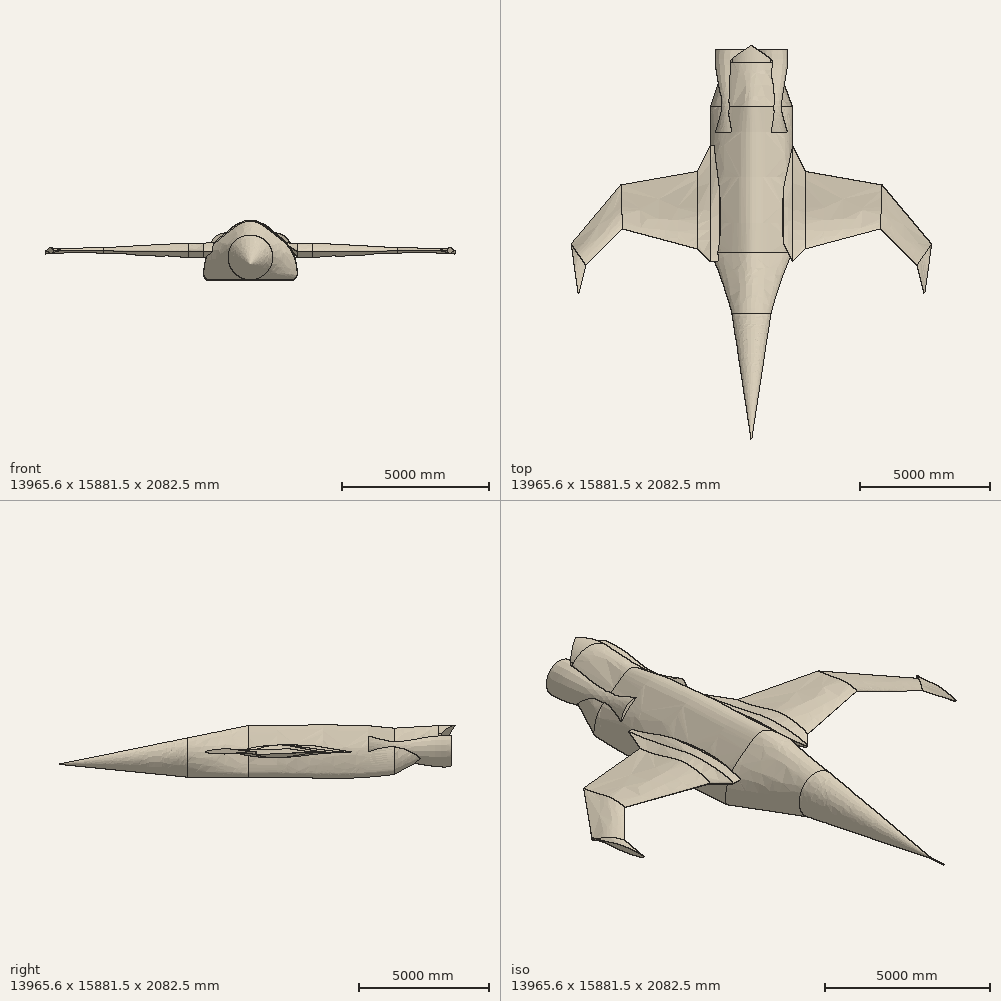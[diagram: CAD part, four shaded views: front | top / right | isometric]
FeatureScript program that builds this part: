
annotation { "Feature Type Name" : "Feature", "Feature Type Description" : "" }
export const myFeature = defineFeature(function(context is Context, id is Id, definition is map)
    precondition{}
    {
        {
            var Q0;
            Q0=qCreatedBy(makeId("Right.planeOp"),FACE);
            var sketch = newSketch(context, id + "F0", { "sketchPlane" : qUnion([Q0])});
            skLineSegment(sketch, "E0", {"start": v(0, 0) * mm, "end": v(-1750, 0) * mm});
            skLineSegment(sketch, "E1", {"start": v(-1750, 0) * mm, "end": v(-3500, 0) * mm});
            skLineSegment(sketch, "E2", {"start": v(-3500, 0) * mm, "end": v(-3500, -1000) * mm});
            skLineSegment(sketch, "E3", {"start": v(-3500, -1000) * mm, "end": v(-8500, -1000) * mm});
            skLineSegment(sketch, "E4", {"start": v(-8500, -1000) * mm, "end": v(-8500, -499.31) * mm});
            skLineSegment(sketch, "E5", {"start": v(-1151.4, 0) * mm, "end": v(-1151.4, 1000) * mm});
            skLineSegment(sketch, "E6", {"start": v(-1151.4, 1000) * mm, "end": v(-8500, -499.31) * mm});
            skLineSegment(sketch, "E7", {"start": v(-8500, -499.31) * mm, "end": v(-3500, -1000) * mm});
            skLineSegment(sketch, "E8", {"start": v(-3500, 0) * mm, "end": v(-3500, 520.82) * mm});
            skLineSegment(sketch, "E9", {"start": v(-8500, -499.31) * mm, "end": v(-8450, -499.31) * mm});
            skLineSegment(sketch, "E10", {"start": v(-8450, -499.31) * mm, "end": v(-8450, -489.1) * mm});
            skLineSegment(sketch, "E11", {"start": v(-8450, -499.31) * mm, "end": v(-8450, -504.32) * mm});
            skSolve(sketch);
        }
        {
            var Q0;
            Q0=sQuery(id+"F0.wireOp",EDGE,"E5");
            cPlane(context, id + "F1", {"entities" : qUnion([Q0]), "cplaneType" : CPlaneType.LINE_ANGLE, "offset" : 25 * mm, "angle" : 90 * degree, "oppositeDirection" : true, "width" : 150 * mm, "height" : 150 * mm});
        }
        {
            var Q0;
            Q0=qCreatedBy(id+"F1.planeOp",FACE);
            var sketch = newSketch(context, id + "F2", { "sketchPlane" : qUnion([Q0])});
            skLineSegment(sketch, "E12.top", {"start": v(-1394.2, -1000) * mm, "end": v(1394.2, -1000) * mm});
            skPoint(sketch, "E12.middle", {"position": v(0, 0) * mm});
            skFitSpline(sketch, "E13", {"points": [v(-1600, -1000) * mm, v(-848, 530) * mm, v(0, 1000) * mm, v(848, 530) * mm, v(1600, -1000) * mm], "startDerivative": vector(0, 10524.75) * mm, "endDerivative": vector(0, -10524.75) * mm});
            skArc(sketch, "E14", {"start": v(-735.27, 618.52) * mm, "mid": v(-1273.27, 435.52) * mm, "end": v(-1440.68, -107.53) * mm});
            skArc(sketch, "E15", {"start": v(1440.68, -107.53) * mm, "mid": v(1273.27, 435.52) * mm, "end": v(735.27, 618.52) * mm});
            skFitSpline(sketch, "E16.trimOffspring", {"points": [v(-1600, -1000) * mm, v(-848, 530) * mm, v(0, 1000) * mm, v(848, 530) * mm, v(1600, -1000) * mm], "startDerivative": vector(0, 10524.75) * mm, "endDerivative": vector(0, -10524.75) * mm});
            skFitSpline(sketch, "E17.trimOffspring", {"points": [v(-1600, -1000) * mm, v(-848, 530) * mm, v(0, 1000) * mm, v(848, 530) * mm, v(1600, -1000) * mm], "startDerivative": vector(0, 10524.75) * mm, "endDerivative": vector(0, -10524.75) * mm});
            skArc(sketch, "E18.filletArc", {"start": v(-1593.82, -787.83) * mm, "mid": v(-1539.85, -937.05) * mm, "end": v(-1394.2, -1000) * mm});
            skArc(sketch, "E19.filletArc", {"start": v(1394.2, -1000) * mm, "mid": v(1539.85, -937.05) * mm, "end": v(1593.82, -787.83) * mm});
            skSolve(sketch);
        }
        {
            var Q0;
            Q0=qCreatedBy(makeId("Front.planeOp"),FACE);
            var sketch = newSketch(context, id + "F3", { "sketchPlane" : qUnion([Q0])});
            skLineSegment(sketch, "E20.top", {"start": v(-1394.2, -1000) * mm, "end": v(1394.2, -1000) * mm});
            skPoint(sketch, "E20.middle", {"position": v(0, 0) * mm});
            skFitSpline(sketch, "E21", {"points": [v(-1600, -1000) * mm, v(-848, 530) * mm, v(0, 1000) * mm, v(848, 530) * mm, v(1600, -1000) * mm], "startDerivative": vector(0, 10524.75) * mm, "endDerivative": vector(0, -10524.75) * mm});
            skArc(sketch, "E22", {"start": v(-735.27, 618.52) * mm, "mid": v(-1273.27, 435.52) * mm, "end": v(-1440.68, -107.53) * mm});
            skArc(sketch, "E23", {"start": v(1440.68, -107.53) * mm, "mid": v(1273.27, 435.52) * mm, "end": v(735.27, 618.52) * mm});
            skFitSpline(sketch, "E24.trimOffspring", {"points": [v(-1600, -1000) * mm, v(-848, 530) * mm, v(0, 1000) * mm, v(848, 530) * mm, v(1600, -1000) * mm], "startDerivative": vector(0, 10524.75) * mm, "endDerivative": vector(0, -10524.75) * mm});
            skFitSpline(sketch, "E25.trimOffspring", {"points": [v(-1600, -1000) * mm, v(-848, 530) * mm, v(0, 1000) * mm, v(848, 530) * mm, v(1600, -1000) * mm], "startDerivative": vector(0, 10524.75) * mm, "endDerivative": vector(0, -10524.75) * mm});
            skArc(sketch, "E26.filletArc", {"start": v(-1593.82, -787.83) * mm, "mid": v(-1539.85, -937.05) * mm, "end": v(-1394.2, -1000) * mm});
            skArc(sketch, "E27.filletArc", {"start": v(1394.2, -1000) * mm, "mid": v(1539.85, -937.05) * mm, "end": v(1593.82, -787.83) * mm});
            skSolve(sketch);
        }
        {
            var Q0;
            Q0=qCreatedBy(makeId("Front.planeOp"),FACE);
            cPlane(context, id + "F4", {"entities" : qUnion([Q0]), "cplaneType" : CPlaneType.OFFSET, "offset" : 3500 * mm, "oppositeDirection" : true, "width" : 150 * mm, "height" : 150 * mm});
        }
        {
            var Q0;
            Q0=qCreatedBy(id+"F4.planeOp",FACE);
            var sketch = newSketch(context, id + "F5", { "sketchPlane" : qUnion([Q0])});
            skLineSegment(sketch, "E28.top", {"start": v(-1394.2, -1000) * mm, "end": v(1394.2, -1000) * mm});
            skPoint(sketch, "E28.middle", {"position": v(0, 0) * mm});
            skFitSpline(sketch, "E29", {"points": [v(-1600, -1000) * mm, v(-848, 530) * mm, v(0, 1000) * mm, v(848, 530) * mm, v(1600, -1000) * mm], "startDerivative": vector(0, 10524.75) * mm, "endDerivative": vector(0, -10524.75) * mm});
            skArc(sketch, "E30", {"start": v(-735.27, 618.52) * mm, "mid": v(-1273.27, 435.52) * mm, "end": v(-1440.68, -107.53) * mm});
            skArc(sketch, "E31", {"start": v(1440.68, -107.53) * mm, "mid": v(1273.27, 435.52) * mm, "end": v(735.27, 618.52) * mm});
            skFitSpline(sketch, "E32.trimOffspring", {"points": [v(-1600, -1000) * mm, v(-848, 530) * mm, v(0, 1000) * mm, v(848, 530) * mm, v(1600, -1000) * mm], "startDerivative": vector(0, 10524.75) * mm, "endDerivative": vector(0, -10524.75) * mm});
            skFitSpline(sketch, "E33.trimOffspring", {"points": [v(-1600, -1000) * mm, v(-848, 530) * mm, v(0, 1000) * mm, v(848, 530) * mm, v(1600, -1000) * mm], "startDerivative": vector(0, 10524.75) * mm, "endDerivative": vector(0, -10524.75) * mm});
            skArc(sketch, "E34.filletArc", {"start": v(-1593.82, -787.83) * mm, "mid": v(-1539.85, -937.05) * mm, "end": v(-1394.2, -1000) * mm});
            skArc(sketch, "E35.filletArc", {"start": v(1394.2, -1000) * mm, "mid": v(1539.85, -937.05) * mm, "end": v(1593.82, -787.83) * mm});
            skSolve(sketch);
        }
        {
            var Q0;
            Q0=qCreatedBy(makeId("Front.planeOp"),FACE);
            cPlane(context, id + "F6", {"entities" : qUnion([Q0]), "cplaneType" : CPlaneType.OFFSET, "offset" : 4500 * mm, "oppositeDirection" : true, "width" : 150 * mm, "height" : 150 * mm});
        }
        {
            var Q0;
            Q0=qCreatedBy(id+"F6.planeOp",FACE);
            var sketch = newSketch(context, id + "F7", { "sketchPlane" : qUnion([Q0])});
            skLineSegment(sketch, "E36.top", {"start": v(-1413.07, -900) * mm, "end": v(1413.07, -900) * mm});
            skPoint(sketch, "E36.middle", {"position": v(0, 0) * mm});
            skFitSpline(sketch, "E37", {"points": [v(-1600, -900) * mm, v(-784.42, 441.24) * mm, v(0, 900) * mm, v(784.42, 441.24) * mm, v(1600, -900) * mm], "startDerivative": vector(0, 9508.62) * mm, "endDerivative": vector(0, -9508.62) * mm});
            skArc(sketch, "E38", {"start": v(-719.25, 488.69) * mm, "mid": v(-1131.76, 394.84) * mm, "end": v(-1324.66, 18.33) * mm});
            skArc(sketch, "E39", {"start": v(1324.66, 18.33) * mm, "mid": v(1131.76, 394.84) * mm, "end": v(719.25, 488.69) * mm});
            skFitSpline(sketch, "E40.trimOffspring", {"points": [v(-1600, -900) * mm, v(-784.42, 441.24) * mm, v(0, 900) * mm, v(784.42, 441.24) * mm, v(1600, -900) * mm], "startDerivative": vector(0, 9508.62) * mm, "endDerivative": vector(0, -9508.62) * mm});
            skFitSpline(sketch, "E41.trimOffspring", {"points": [v(-1600, -900) * mm, v(-784.42, 441.24) * mm, v(0, 900) * mm, v(784.42, 441.24) * mm, v(1600, -900) * mm], "startDerivative": vector(0, 9508.62) * mm, "endDerivative": vector(0, -9508.62) * mm});
            skArc(sketch, "E42.filletArc", {"start": v(-1592.48, -705.43) * mm, "mid": v(-1545.4, -842.02) * mm, "end": v(-1413.07, -900) * mm});
            skArc(sketch, "E43.filletArc", {"start": v(1413.07, -900) * mm, "mid": v(1545.4, -842.02) * mm, "end": v(1592.48, -705.43) * mm});
            skLineSegment(sketch, "E44", {"start": v(-719.25, 488.69) * mm, "end": v(-1324.66, 18.33) * mm, "construction": true});
            skLineSegment(sketch, "E45", {"start": v(719.25, 488.69) * mm, "end": v(1324.66, 18.33) * mm, "construction": true});
            skSolve(sketch);
        }
        {
            var Q0;
            Q0=qCreatedBy(makeId("Front.planeOp"),FACE);
            cPlane(context, id + "F8", {"entities" : qUnion([Q0]), "cplaneType" : CPlaneType.OFFSET, "offset" : 6232.05 * mm, "oppositeDirection" : true, "width" : 150 * mm, "height" : 150 * mm});
        }
        {
            var Q0;
            Q0=qCreatedBy(id+"F8.planeOp",FACE);
            var sketch = newSketch(context, id + "F9", { "sketchPlane" : qUnion([Q0])});
            skArc(sketch, "E46", {"start": v(998.61, 52.63) * mm, "mid": v(0, 1000) * mm, "end": v(-998.61, 52.63) * mm});
            skLineSegment(sketch, "E47", {"start": v(0, 0) * mm, "end": v(-948.68, 0) * mm});
            skLineSegment(sketch, "E48", {"start": v(0, 0) * mm, "end": v(948.68, 0) * mm});
            skLineSegment(sketch, "E49", {"start": v(0, 1000) * mm, "end": v(0, 675) * mm, "construction": true});
            skLineSegment(sketch, "E50", {"start": v(0, 675) * mm, "end": v(-737.82, 675) * mm, "construction": true});
            skLineSegment(sketch, "E51", {"start": v(0, 675) * mm, "end": v(737.82, 675) * mm, "construction": true});
            skPoint(sketch, "E52.visualSharp", {"position": v(-1000, 0) * mm});
            skArc(sketch, "E52.filletArc", {"start": v(-998.61, 52.63) * mm, "mid": v(-984.96, 15.59) * mm, "end": v(-948.68, 0) * mm});
            skPoint(sketch, "E53.visualSharp", {"position": v(1000, 0) * mm});
            skArc(sketch, "E53.filletArc", {"start": v(948.68, 0) * mm, "mid": v(984.96, 15.59) * mm, "end": v(998.61, 52.63) * mm});
            skSolve(sketch);
        }
        {
            var Q0;
            Q0=makeQuery(id+"F2.imprint","IMPRINT",FACE,{"disambiguationData":[TD([[makeQuery(id+"F2.imprint","IMPRINT",EDGE,{"derivedFrom":sQuery(id+"F2.wireOp",EDGE,"E12.top")}),1.0]])]});
            var Q1;
            Q1=makeQuery(id+"F3.imprint","IMPRINT",FACE,{"disambiguationData":[TD([[makeQuery(id+"F3.imprint","IMPRINT",EDGE,{"derivedFrom":sQuery(id+"F3.wireOp",EDGE,"E20.top")}),1.0]])]});
            var Q2;
            Q2=makeQuery(id+"F5.imprint","IMPRINT",FACE,{"disambiguationData":[TD([[makeQuery(id+"F5.imprint","IMPRINT",EDGE,{"derivedFrom":sQuery(id+"F5.wireOp",EDGE,"E28.top")}),1.0]])]});
            var Q3;
            Q3=makeQuery(id+"F7.imprint","IMPRINT",FACE,{"disambiguationData":[TD([[makeQuery(id+"F7.imprint","IMPRINT",EDGE,{"derivedFrom":sQuery(id+"F7.wireOp",EDGE,"E36.top")}),1.0]])]});
            loft(context, id + "F10", {"sheetProfilesArray" : [{ "sheetProfileEntities" : qUnion([Q0]) }, { "sheetProfileEntities" : qUnion([Q1]) }, { "sheetProfileEntities" : qUnion([Q2]) }, { "sheetProfileEntities" : qUnion([Q3]) }]});
        }
        {
            var Q0;
            Q0=sQuery(id+"F7.wireOp",EDGE,"E44");
            var Q1;
            Q1=sQuery(id+"F9.wireOp",VERTEX,"E50.end");
            cPlane(context, id + "F11", {"entities" : qUnion([Q0, Q1]), "cplaneType" : CPlaneType.LINE_ANGLE, "offset" : 25 * mm, "angle" : 180 * degree, "width" : 150 * mm, "height" : 150 * mm});
        }
        {
            var Q0;
            Q0=qCreatedBy(id+"F11.planeOp",FACE);
            var sketch = newSketch(context, id + "F12", { "sketchPlane" : qUnion([Q0])});
            skLineSegment(sketch, "E54", {"start": v(-589.34, 4526.34) * mm, "end": v(-612.8, 6268.32) * mm});
            skLineSegment(sketch, "E55", {"start": v(-1354.08, 4472.19) * mm, "end": v(-612.8, 6268.32) * mm});
            skSolve(sketch);
        }
        {
            var Q0;
            Q0=sQuery(id+"F7.wireOp",EDGE,"E45");
            var Q1;
            Q1=sQuery(id+"F9.wireOp",VERTEX,"E51.end");
            cPlane(context, id + "F13", {"entities" : qUnion([Q0, Q1]), "cplaneType" : CPlaneType.LINE_ANGLE, "offset" : 25 * mm, "angle" : 0 * degree, "width" : 150 * mm, "height" : 150 * mm});
        }
        {
            var Q0;
            Q0=qCreatedBy(id+"F13.planeOp",FACE);
            var sketch = newSketch(context, id + "F14", { "sketchPlane" : qUnion([Q0])});
            skLineSegment(sketch, "E56", {"start": v(589.34, 4526.34) * mm, "end": v(612.8, 6268.32) * mm});
            skLineSegment(sketch, "E57", {"start": v(1354.08, 4472.19) * mm, "end": v(612.8, 6268.32) * mm});
            skSolve(sketch);
        }
        {
            var Q1;
            Q1=makeQuery(id+"F10.opLoft","CAP_FACE",FACE,{"disambiguationData":[OSD([makeQuery(id+"F7.imprint","IMPRINT",FACE,{"disambiguationData":[TD([[makeQuery(id+"F7.imprint","IMPRINT",EDGE,{"derivedFrom":sQuery(id+"F7.wireOp",EDGE,"E36.top")}),1.0]])]})])],"isStart":true});
            var Q2;
            Q2=makeQuery(id+"F9.imprint","IMPRINT",FACE,{"disambiguationData":[TD([[makeQuery(id+"F9.imprint","IMPRINT",EDGE,{"derivedFrom":sQuery(id+"F9.wireOp",EDGE,"E46")}),1.0]])]});
            var Q3;
            Q3=sQuery(id+"F12.wireOp",EDGE,"E54");
            var Q4;
            Q4=sQuery(id+"F14.wireOp",EDGE,"E56");
            loft(context, id + "F15", {"operationType" : NewBodyOperationType.ADD, "addGuides" : true, "sheetProfilesArray" : [{ "sheetProfileEntities" : qUnion([Q1]) }, { "sheetProfileEntities" : qUnion([Q2]) }], "guidesArray" : [{ "guideEntities" : qUnion([Q3]), "guideDerivativeType" : LoftGuideDerivativeType.DEFAULT, "guideDerivativeMagnitude" : 1 }, { "guideEntities" : qUnion([Q4]), "guideDerivativeType" : LoftGuideDerivativeType.DEFAULT, "guideDerivativeMagnitude" : 1 }]});
        }
        {
            var Q0;
            Q0=makeQuery(id+"F15.opLoft","CAP_FACE",FACE,{"disambiguationData":[OSD([makeQuery(id+"F9.imprint","IMPRINT",FACE,{"disambiguationData":[TD([[makeQuery(id+"F9.imprint","IMPRINT",EDGE,{"derivedFrom":sQuery(id+"F9.wireOp",EDGE,"E46")}),1.0]])]})])],"isStart":true});
            extrude(context, id + "F16", {"entities" : qUnion([Q0]), "operationType" : NewBodyOperationType.ADD, "depth" : 649.4 * mm, "offsetDistance" : 25 * mm});
        }
        {
            var Q0;
            Q0=qCreatedBy(makeId("Right.planeOp"),FACE);
            var sketch = newSketch(context, id + "F17", { "sketchPlane" : qUnion([Q0])});
            skLineSegment(sketch, "E58", {"start": v(0, 0) * mm, "end": v(4500, 0) * mm});
            skLineSegment(sketch, "E59", {"start": v(4500, 0) * mm, "end": v(6232.05, 0) * mm});
            skLineSegment(sketch, "E60", {"start": v(4500, 0) * mm, "end": v(4500, 1000) * mm});
            skLineSegment(sketch, "E61", {"start": v(4500, 1000) * mm, "end": v(6881.46, 1000) * mm});
            skLineSegment(sketch, "E62", {"start": v(6881.46, 1000) * mm, "end": v(6881.46, -1000) * mm});
            skLineSegment(sketch, "E63", {"start": v(6881.46, 1000) * mm, "end": v(6232.05, 0) * mm});
            skLineSegment(sketch, "E64", {"start": v(6232.05, 0) * mm, "end": v(5582.64, -1000) * mm});
            skLineSegment(sketch, "E65", {"start": v(5582.64, -1000) * mm, "end": v(6881.46, -1000) * mm});
            skSolve(sketch);
        }
        {
            var Q0;
            Q0=makeQuery(id+"F17.imprint","IMPRINT",FACE,{"disambiguationData":[TD([[makeQuery(id+"F17.imprint","IMPRINT",EDGE,{"derivedFrom":sQuery(id+"F17.wireOp",EDGE,"E62")}),-1.0]])]});
            var Q1;
            Q1=sQuery(id+"F17.wireOp",EDGE,"E61");
            revolve(context, id + "F18", {"operationType" : NewBodyOperationType.REMOVE, "entities" : qUnion([Q0]), "axis" : qUnion([Q1]), "revolveType" : RevolveType.SYMMETRIC, "oppositeDirection" : true, "angle" : 182 * degree});
        }
        {
            var Q0;
            Q0=qCreatedBy(id+"F1.planeOp",FACE);
            var sketch = newSketch(context, id + "F19", { "sketchPlane" : qUnion([Q0])});
            skLineSegment(sketch, "E66.top", {"start": v(-1394.2, -1000) * mm, "end": v(1394.2, -1000) * mm});
            skPoint(sketch, "E66.middle", {"position": v(0, 0) * mm});
            skFitSpline(sketch, "E67", {"points": [v(-1600, -1000) * mm, v(-848, 530) * mm, v(0, 1000) * mm, v(848, 530) * mm, v(1600, -1000) * mm], "startDerivative": vector(0, 10524.75) * mm, "endDerivative": vector(0, -10524.75) * mm});
            skArc(sketch, "E68.filletArc", {"start": v(-1593.82, -787.83) * mm, "mid": v(-1539.85, -937.05) * mm, "end": v(-1394.2, -1000) * mm});
            skArc(sketch, "E69.filletArc", {"start": v(1394.2, -1000) * mm, "mid": v(1539.85, -937.05) * mm, "end": v(1593.82, -787.83) * mm});
            skLineSegment(sketch, "E70", {"start": v(-1593.82, -787.83) * mm, "end": v(-1394.2, -1000) * mm, "construction": true});
            skLineSegment(sketch, "E71", {"start": v(1593.82, -787.83) * mm, "end": v(1394.2, -1000) * mm, "construction": true});
            skSolve(sketch);
        }
        {
            var Q0;
            Q0=qCreatedBy(makeId("Front.planeOp"),FACE);
            cPlane(context, id + "F20", {"entities" : qUnion([Q0]), "cplaneType" : CPlaneType.OFFSET, "offset" : 3500 * mm, "width" : 150 * mm, "height" : 150 * mm});
        }
        {
            var Q0;
            Q0=qCreatedBy(id+"F20.planeOp",FACE);
            var sketch = newSketch(context, id + "F21", { "sketchPlane" : qUnion([Q0])});
            skCircle(sketch, "E72", {"center": v(0, -239.59) * mm, "radius": 760.41 * mm});
            skLineSegment(sketch, "E73", {"start": v(0, -1000) * mm, "end": v(0, -800) * mm, "construction": true});
            skLineSegment(sketch, "E74", {"start": v(0, -800) * mm, "end": v(-513.97, -800) * mm, "construction": true});
            skLineSegment(sketch, "E75", {"start": v(0, -800) * mm, "end": v(513.97, -800) * mm, "construction": true});
            skSolve(sketch);
        }
        {
            var Q0;
            Q0=qCreatedBy(makeId("Front.planeOp"),FACE);
            cPlane(context, id + "F22", {"entities" : qUnion([Q0]), "cplaneType" : CPlaneType.OFFSET, "offset" : 8450 * mm, "width" : 150 * mm, "height" : 150 * mm});
        }
        {
            var Q0;
            Q0=qCreatedBy(id+"F22.planeOp",FACE);
            var sketch = newSketch(context, id + "F23", { "sketchPlane" : qUnion([Q0])});
            skCircle(sketch, "E76", {"center": v(0, -496.71) * mm, "radius": 7.6 * mm});
            skSolve(sketch);
        }
        {
            var Q0;
            Q0=sQuery(id+"F19.wireOp",EDGE,"E70");
            var Q1;
            Q1=sQuery(id+"F21.wireOp",VERTEX,"E74.end");
            cPlane(context, id + "F24", {"entities" : qUnion([Q0, Q1]), "cplaneType" : CPlaneType.LINE_ANGLE, "offset" : 25 * mm, "angle" : 0 * degree, "width" : 150 * mm, "height" : 150 * mm});
        }
        {
            var Q0;
            Q0=qCreatedBy(id+"F24.planeOp",FACE);
            var sketch = newSketch(context, id + "F25", { "sketchPlane" : qUnion([Q0])});
            skLineSegment(sketch, "E77", {"start": v(3032.27, -230.44) * mm, "end": v(558.11, 518.4) * mm});
            skLineSegment(sketch, "E78", {"start": v(3032.27, -230.44) * mm, "end": v(558.11, 227.09) * mm});
            skSolve(sketch);
        }
        {
            var Q0;
            Q0=sQuery(id+"F19.wireOp",EDGE,"E71");
            var Q1;
            Q1=sQuery(id+"F21.wireOp",VERTEX,"E75.end");
            cPlane(context, id + "F26", {"entities" : qUnion([Q0, Q1]), "cplaneType" : CPlaneType.LINE_ANGLE, "offset" : 25 * mm, "angle" : 180 * degree, "width" : 150 * mm, "height" : 150 * mm});
        }
        {
            var Q0;
            Q0=qCreatedBy(id+"F26.planeOp",FACE);
            var sketch = newSketch(context, id + "F27", { "sketchPlane" : qUnion([Q0])});
            skLineSegment(sketch, "E79", {"start": v(-3032.27, -230.44) * mm, "end": v(-558.11, 518.4) * mm});
            skLineSegment(sketch, "E80", {"start": v(-3032.27, -230.44) * mm, "end": v(-558.11, 227.09) * mm});
            skSolve(sketch);
        }
        {
            var Q1;
            Q1=makeQuery(id+"F19.imprint","IMPRINT",FACE,{"disambiguationData":[TD([[makeQuery(id+"F19.imprint","IMPRINT",EDGE,{"derivedFrom":sQuery(id+"F19.wireOp",EDGE,"E66.top")}),1.0]])]});
            var Q2;
            Q2=makeQuery(id+"F21.imprint","IMPRINT",FACE,{"disambiguationData":[TD([[makeQuery(id+"F21.imprint","IMPRINT",EDGE,{"derivedFrom":sQuery(id+"F21.wireOp",EDGE,"E72")}),1.0]])]});
            var Q3;
            Q3=sQuery(id+"F25.wireOp",EDGE,"E77");
            var Q4;
            Q4=sQuery(id+"F27.wireOp",EDGE,"E79");
            loft(context, id + "F28", {"operationType" : NewBodyOperationType.ADD, "addGuides" : true, "sheetProfilesArray" : [{ "sheetProfileEntities" : qUnion([Q1]) }, { "sheetProfileEntities" : qUnion([Q2]) }], "guidesArray" : [{ "guideEntities" : qUnion([Q3]), "guideDerivativeType" : LoftGuideDerivativeType.DEFAULT, "guideDerivativeMagnitude" : 1 }, { "guideEntities" : qUnion([Q4]), "guideDerivativeType" : LoftGuideDerivativeType.DEFAULT, "guideDerivativeMagnitude" : 1 }]});
        }
        {
            var Q1;
            Q1=makeQuery(id+"F28.opLoft","CAP_FACE",FACE,{"disambiguationData":[OSD([makeQuery(id+"F21.imprint","IMPRINT",FACE,{"disambiguationData":[TD([[makeQuery(id+"F21.imprint","IMPRINT",EDGE,{"derivedFrom":sQuery(id+"F21.wireOp",EDGE,"E72")}),1.0]])]})])],"isStart":true});
            var Q2;
            Q2=makeQuery(id+"F23.imprint","IMPRINT",FACE,{"disambiguationData":[TD([[makeQuery(id+"F23.imprint","IMPRINT",EDGE,{"derivedFrom":sQuery(id+"F23.wireOp",EDGE,"E76")}),1.0]])]});
            loft(context, id + "F29", {"operationType" : NewBodyOperationType.ADD, "sheetProfilesArray" : [{ "sheetProfileEntities" : qUnion([Q1]) }, { "sheetProfileEntities" : qUnion([Q2]) }]});
        }
        {
            var Q0;
            Q0=makeQuery(id+"F29.opLoft","CAP_FACE",FACE,{"disambiguationData":[OSD([makeQuery(id+"F23.imprint","IMPRINT",FACE,{"disambiguationData":[TD([[makeQuery(id+"F23.imprint","IMPRINT",EDGE,{"derivedFrom":sQuery(id+"F23.wireOp",EDGE,"E76")}),1.0]])]})])],"isStart":true});
            extrude(context, id + "F30", {"entities" : qUnion([Q0]), "operationType" : NewBodyOperationType.ADD, "depth" : 550 * mm, "offsetDistance" : 25 * mm});
        }
        {
            var Q0;
            Q0=qCreatedBy(makeId("Front.planeOp"),FACE);
            cPlane(context, id + "F31", {"entities" : qUnion([Q0]), "cplaneType" : CPlaneType.OFFSET, "offset" : 3500 * mm, "oppositeDirection" : true, "width" : 150 * mm, "height" : 150 * mm});
        }
        {
            var Q0;
            Q0=qCreatedBy(id+"F31.planeOp",FACE);
            var sketch = newSketch(context, id + "F32", { "sketchPlane" : qUnion([Q0])});
            skCircle(sketch, "E81", {"center": v(-800, 0) * mm, "radius": 600 * mm});
            skCircle(sketch, "E82", {"center": v(800, 0) * mm, "radius": 600 * mm});
            skSolve(sketch);
        }
        {
            var Q0;
            Q0=qCreatedBy(makeId("Front.planeOp"),FACE);
            cPlane(context, id + "F33", {"entities" : qUnion([Q0]), "cplaneType" : CPlaneType.OFFSET, "offset" : 4500 * mm, "oppositeDirection" : true, "width" : 150 * mm, "height" : 150 * mm});
        }
        {
            var Q0;
            Q0=qCreatedBy(id+"F33.planeOp",FACE);
            var sketch = newSketch(context, id + "F34", { "sketchPlane" : qUnion([Q0])});
            skCircle(sketch, "E83", {"center": v(-800, 0) * mm, "radius": 400 * mm});
            skCircle(sketch, "E84", {"center": v(800, 0) * mm, "radius": 400 * mm});
            skSolve(sketch);
        }
        {
            var Q0;
            Q0=qCreatedBy(makeId("Front.planeOp"),FACE);
            cPlane(context, id + "F35", {"entities" : qUnion([Q0]), "cplaneType" : CPlaneType.OFFSET, "offset" : 6232.05 * mm, "oppositeDirection" : true, "width" : 150 * mm, "height" : 150 * mm});
        }
        {
            var Q0;
            Q0=qCreatedBy(id+"F35.planeOp",FACE);
            var sketch = newSketch(context, id + "F36", { "sketchPlane" : qUnion([Q0])});
            skCircle(sketch, "E85", {"center": v(-800, 0) * mm, "radius": 600 * mm});
            skCircle(sketch, "E86", {"center": v(800, 0) * mm, "radius": 600 * mm});
            skSolve(sketch);
        }
        {
            var Q0;
            Q0=qCreatedBy(makeId("Front.planeOp"),FACE);
            cPlane(context, id + "F37", {"entities" : qUnion([Q0]), "cplaneType" : CPlaneType.OFFSET, "offset" : 6732.05 * mm, "oppositeDirection" : true, "width" : 150 * mm, "height" : 150 * mm});
        }
        {
            var Q0;
            Q0=qCreatedBy(id+"F37.planeOp",FACE);
            var sketch = newSketch(context, id + "F38", { "sketchPlane" : qUnion([Q0])});
            skCircle(sketch, "E87", {"center": v(-800, 0) * mm, "radius": 600 * mm});
            skCircle(sketch, "E88", {"center": v(800, 0) * mm, "radius": 600 * mm});
            skSolve(sketch);
        }
        {
            var Q0;
            Q0=makeQuery(id+"F32.imprint","IMPRINT",FACE,{"disambiguationData":[TD([[makeQuery(id+"F32.imprint","IMPRINT",EDGE,{"derivedFrom":sQuery(id+"F32.wireOp",EDGE,"E81")}),1.0]])]});
            var Q1;
            Q1=makeQuery(id+"F34.imprint","IMPRINT",FACE,{"disambiguationData":[TD([[makeQuery(id+"F34.imprint","IMPRINT",EDGE,{"derivedFrom":sQuery(id+"F34.wireOp",EDGE,"E83")}),1.0]])]});
            var Q2;
            Q2=makeQuery(id+"F36.imprint","IMPRINT",FACE,{"disambiguationData":[TD([[makeQuery(id+"F36.imprint","IMPRINT",EDGE,{"derivedFrom":sQuery(id+"F36.wireOp",EDGE,"E85")}),1.0]])]});
            var Q3;
            Q3=makeQuery(id+"F38.imprint","IMPRINT",FACE,{"disambiguationData":[TD([[makeQuery(id+"F38.imprint","IMPRINT",EDGE,{"derivedFrom":sQuery(id+"F38.wireOp",EDGE,"E87")}),1.0]])]});
            loft(context, id + "F39", {"sheetProfilesArray" : [{ "sheetProfileEntities" : qUnion([Q0]) }, { "sheetProfileEntities" : qUnion([Q1]) }, { "sheetProfileEntities" : qUnion([Q2]) }, { "sheetProfileEntities" : qUnion([Q3]) }]});
        }
        {
            var Q0;
            Q0=makeQuery(id+"F32.imprint","IMPRINT",FACE,{"disambiguationData":[TD([[makeQuery(id+"F32.imprint","IMPRINT",EDGE,{"derivedFrom":sQuery(id+"F32.wireOp",EDGE,"E82")}),1.0]])]});
            var Q1;
            Q1=makeQuery(id+"F34.imprint","IMPRINT",FACE,{"disambiguationData":[TD([[makeQuery(id+"F34.imprint","IMPRINT",EDGE,{"derivedFrom":sQuery(id+"F34.wireOp",EDGE,"E84")}),1.0]])]});
            var Q2;
            Q2=makeQuery(id+"F36.imprint","IMPRINT",FACE,{"disambiguationData":[TD([[makeQuery(id+"F36.imprint","IMPRINT",EDGE,{"derivedFrom":sQuery(id+"F36.wireOp",EDGE,"E86")}),1.0]])]});
            var Q3;
            Q3=makeQuery(id+"F38.imprint","IMPRINT",FACE,{"disambiguationData":[TD([[makeQuery(id+"F38.imprint","IMPRINT",EDGE,{"derivedFrom":sQuery(id+"F38.wireOp",EDGE,"E88")}),1.0]])]});
            loft(context, id + "F40", {"sheetProfilesArray" : [{ "sheetProfileEntities" : qUnion([Q0]) }, { "sheetProfileEntities" : qUnion([Q1]) }, { "sheetProfileEntities" : qUnion([Q2]) }, { "sheetProfileEntities" : qUnion([Q3]) }]});
        }
        {
            var Q0;
            Q0=qCreatedBy(makeId("Top.planeOp"),FACE);
            var sketch = newSketch(context, id + "F41", { "sketchPlane" : qUnion([Q0])});
            skLineSegment(sketch, "E89", {"start": v(0, 0) * mm, "end": v(-1250, 0) * mm});
            skLineSegment(sketch, "E90", {"start": v(-1250, 0) * mm, "end": v(-2100, 0) * mm});
            skLineSegment(sketch, "E91", {"start": v(-2100, 0) * mm, "end": v(-2100, -1000) * mm});
            skLineSegment(sketch, "E92", {"start": v(-2100, 0) * mm, "end": v(-2100, 2000) * mm});
            skLineSegment(sketch, "E93", {"start": v(-2100, -1000) * mm, "end": v(-4997.78, -223.54) * mm});
            skLineSegment(sketch, "E94", {"start": v(-2100, 2000) * mm, "end": v(-5054.42, 1479.06) * mm});
            skLineSegment(sketch, "E95", {"start": v(-4997.78, -223.54) * mm, "end": v(-5054.42, 1479.06) * mm});
            skLineSegment(sketch, "E96", {"start": v(-4997.78, -223.54) * mm, "end": v(-6412, -1637.76) * mm});
            skLineSegment(sketch, "E97", {"start": v(-5054.42, 1479.06) * mm, "end": v(-6982.79, -819.08) * mm});
            skLineSegment(sketch, "E98", {"start": v(-6412, -1637.76) * mm, "end": v(-6982.79, -819.08) * mm});
            skLineSegment(sketch, "E99", {"start": v(-6412, -1637.76) * mm, "end": v(-6704.44, -2799.61) * mm});
            skLineSegment(sketch, "E100", {"start": v(-6704.44, -2799.61) * mm, "end": v(-6982.79, -819.08) * mm});
            skLineSegment(sketch, "E101", {"start": v(0, 0) * mm, "end": v(1250, 0) * mm});
            skLineSegment(sketch, "E102", {"start": v(1250, 0) * mm, "end": v(2100, 0) * mm});
            skLineSegment(sketch, "E103", {"start": v(2100, 0) * mm, "end": v(2100, -1000) * mm});
            skLineSegment(sketch, "E104", {"start": v(2100, 0) * mm, "end": v(2100, 2000) * mm});
            skLineSegment(sketch, "E105", {"start": v(2100, -1000) * mm, "end": v(4997.78, -223.54) * mm});
            skLineSegment(sketch, "E106", {"start": v(2100, 2000) * mm, "end": v(5054.42, 1479.06) * mm});
            skLineSegment(sketch, "E107", {"start": v(4997.78, -223.54) * mm, "end": v(5054.42, 1479.06) * mm});
            skLineSegment(sketch, "E108", {"start": v(4997.78, -223.54) * mm, "end": v(6412, -1637.76) * mm});
            skLineSegment(sketch, "E109", {"start": v(5054.42, 1479.06) * mm, "end": v(6982.79, -819.08) * mm});
            skLineSegment(sketch, "E110", {"start": v(6412, -1637.76) * mm, "end": v(6982.79, -819.08) * mm});
            skLineSegment(sketch, "E111", {"start": v(6412, -1637.76) * mm, "end": v(6704.44, -2799.61) * mm});
            skLineSegment(sketch, "E112", {"start": v(6704.44, -2799.61) * mm, "end": v(6982.79, -819.08) * mm});
            skSolve(sketch);
        }
        {
            var Q0;
            Q0=qCreatedBy(makeId("Right.planeOp"),FACE);
            var sketch = newSketch(context, id + "F42", { "sketchPlane" : qUnion([Q0])});
            skFitSpline(sketch, "E113", {"points": [v(-1500, -50) * mm, v(0, 250) * mm, v(3000, -50) * mm, v(0, -250) * mm, v(-1500, -50) * mm]});
            skSolve(sketch);
        }
        {
            var Q0;
            Q0=qCreatedBy(makeId("Right.planeOp"),FACE);
            cPlane(context, id + "F43", {"entities" : qUnion([Q0]), "cplaneType" : CPlaneType.OFFSET, "offset" : 1600 * mm, "oppositeDirection" : true, "width" : 150 * mm, "height" : 150 * mm});
        }
        {
            var Q0;
            Q0=qCreatedBy(id+"F43.planeOp",FACE);
            var sketch = newSketch(context, id + "F44", { "sketchPlane" : qUnion([Q0])});
            skFitSpline(sketch, "E114", {"points": [v(-1500, -50) * mm, v(0, 250) * mm, v(3000, -50) * mm], "startDerivative": vector(0, 887.04) * mm, "endDerivative": vector(7705.35, -256.85) * mm});
            skFitSpline(sketch, "E115", {"points": [v(-1500, -50) * mm, v(0, -250) * mm, v(3000, -50) * mm], "startDerivative": vector(0, -722.87) * mm, "endDerivative": vector(7692.49, -256.42) * mm});
            skSolve(sketch);
        }
        {
            var Q0;
            Q0=qCreatedBy(makeId("Right.planeOp"),FACE);
            cPlane(context, id + "F45", {"entities" : qUnion([Q0]), "cplaneType" : CPlaneType.OFFSET, "offset" : 1600 * mm, "width" : 150 * mm, "height" : 150 * mm});
        }
        {
            var Q0;
            Q0=qCreatedBy(id+"F45.planeOp",FACE);
            var sketch = newSketch(context, id + "F46", { "sketchPlane" : qUnion([Q0])});
            skFitSpline(sketch, "E116", {"points": [v(-1500, -50) * mm, v(0, 250) * mm, v(3000, -50) * mm], "startDerivative": vector(0, 887.04) * mm, "endDerivative": vector(7705.35, -256.85) * mm});
            skFitSpline(sketch, "E117", {"points": [v(-1500, -50) * mm, v(0, -250) * mm, v(3000, -50) * mm], "startDerivative": vector(0, -722.87) * mm, "endDerivative": vector(7692.49, -256.42) * mm});
            skSolve(sketch);
        }
        {
            var Q0;
            Q0=qCreatedBy(makeId("Right.planeOp"),FACE);
            cPlane(context, id + "F47", {"entities" : qUnion([Q0]), "cplaneType" : CPlaneType.OFFSET, "offset" : 2100 * mm, "oppositeDirection" : true, "width" : 150 * mm, "height" : 150 * mm});
        }
        {
            var Q0;
            Q0=qCreatedBy(id+"F47.planeOp",FACE);
            var sketch = newSketch(context, id + "F48", { "sketchPlane" : qUnion([Q0])});
            skFitSpline(sketch, "E118", {"points": [v(-1000, -36) * mm, v(0, 250) * mm, v(2000, -36) * mm], "startDerivative": vector(0, 574.5) * mm, "endDerivative": vector(5152.5, -185.5) * mm});
            skFitSpline(sketch, "E119", {"points": [v(-1000, -36) * mm, v(0, -250) * mm, v(2000, -36) * mm], "startDerivative": vector(0, -699.11) * mm, "endDerivative": vector(5139.1, -185) * mm});
            skSolve(sketch);
        }
        {
            var Q0;
            Q0=qCreatedBy(makeId("Right.planeOp"),FACE);
            cPlane(context, id + "F49", {"entities" : qUnion([Q0]), "cplaneType" : CPlaneType.OFFSET, "offset" : 2100 * mm, "width" : 150 * mm, "height" : 150 * mm});
        }
        {
            var Q0;
            Q0=qCreatedBy(id+"F49.planeOp",FACE);
            var sketch = newSketch(context, id + "F50", { "sketchPlane" : qUnion([Q0])});
            skFitSpline(sketch, "E120", {"points": [v(-1000, -36) * mm, v(0, 250) * mm, v(2000, -36) * mm], "startDerivative": vector(0, 574.5) * mm, "endDerivative": vector(5152.5, -185.5) * mm});
            skFitSpline(sketch, "E121", {"points": [v(-1000, -36) * mm, v(0, -250) * mm, v(2000, -36) * mm], "startDerivative": vector(0, -699.11) * mm, "endDerivative": vector(5139.1, -185) * mm});
            skSolve(sketch);
        }
        {
            var Q0;
            Q0=sQuery(id+"F41.wireOp",EDGE,"E95");
            cPlane(context, id + "F51", {"entities" : qUnion([Q0]), "cplaneType" : CPlaneType.LINE_ANGLE, "offset" : 25 * mm, "angle" : 90 * degree, "oppositeDirection" : true, "width" : 150 * mm, "height" : 150 * mm});
        }
        {
            var Q0;
            Q0=qCreatedBy(id+"F51.planeOp",FACE);
            var sketch = newSketch(context, id + "F52", { "sketchPlane" : qUnion([Q0])});
            skFitSpline(sketch, "E122", {"points": [v(57.23, -18) * mm, v(-442.77, 100) * mm, v(-1646.3, -18) * mm], "startDerivative": vector(0, 311.71) * mm, "endDerivative": vector(-2981.97, -89.2) * mm});
            skFitSpline(sketch, "E123", {"points": [v(57.23, -18) * mm, v(-442.77, -100) * mm, v(-1646.3, -18) * mm], "startDerivative": vector(0, -370) * mm, "endDerivative": vector(-2975.3, -89) * mm});
            skSolve(sketch);
        }
        {
            var Q0;
            Q0=sQuery(id+"F41.wireOp",EDGE,"E107");
            cPlane(context, id + "F53", {"entities" : qUnion([Q0]), "cplaneType" : CPlaneType.LINE_ANGLE, "offset" : 25 * mm, "angle" : 90 * degree, "width" : 150 * mm, "height" : 150 * mm});
        }
        {
            var Q0;
            Q0=qCreatedBy(id+"F53.planeOp",FACE);
            var sketch = newSketch(context, id + "F54", { "sketchPlane" : qUnion([Q0])});
            skFitSpline(sketch, "E124", {"points": [v(-57.23, -18) * mm, v(442.77, 100) * mm, v(1646.3, -18) * mm], "startDerivative": vector(0, 311.71) * mm, "endDerivative": vector(2981.97, -89.2) * mm});
            skFitSpline(sketch, "E125", {"points": [v(-57.23, -18) * mm, v(442.77, -100) * mm, v(1646.3, -18) * mm], "startDerivative": vector(0, -370) * mm, "endDerivative": vector(2975.3, -89) * mm});
            skSolve(sketch);
        }
        {
            var Q0;
            Q0=sQuery(id+"F41.wireOp",EDGE,"E98");
            cPlane(context, id + "F55", {"entities" : qUnion([Q0]), "cplaneType" : CPlaneType.LINE_ANGLE, "offset" : 25 * mm, "angle" : 90 * degree, "oppositeDirection" : true, "width" : 150 * mm, "height" : 150 * mm});
        }
        {
            var Q0;
            Q0=qCreatedBy(id+"F55.planeOp",FACE);
            var sketch = newSketch(context, id + "F56", { "sketchPlane" : qUnion([Q0])});
            skFitSpline(sketch, "E126", {"points": [v(-2323.74, 0) * mm, v(-2822.75, 50) * mm, v(-3321.76, -125) * mm], "startDerivative": vector(-1017.94, 211.55) * mm, "endDerivative": vector(-978.27, -458.6) * mm});
            skFitSpline(sketch, "E127", {"points": [v(-2323.74, 0) * mm, v(-2822.75, -50) * mm, v(-3321.76, -125) * mm], "startDerivative": vector(-1000.33, -87.77) * mm, "endDerivative": vector(-995.7, -162.2) * mm});
            skSolve(sketch);
        }
        {
            var Q0;
            Q0=sQuery(id+"F41.wireOp",EDGE,"E110");
            cPlane(context, id + "F57", {"entities" : qUnion([Q0]), "cplaneType" : CPlaneType.LINE_ANGLE, "offset" : 25 * mm, "angle" : 90 * degree, "width" : 150 * mm, "height" : 150 * mm});
        }
        {
            var Q0;
            Q0=qCreatedBy(id+"F57.planeOp",FACE);
            var sketch = newSketch(context, id + "F58", { "sketchPlane" : qUnion([Q0])});
            skFitSpline(sketch, "E128", {"points": [v(2323.74, 0) * mm, v(2822.75, 50) * mm, v(3321.76, -125) * mm], "startDerivative": vector(1017.94, 211.55) * mm, "endDerivative": vector(978.27, -458.6) * mm});
            skFitSpline(sketch, "E129", {"points": [v(2323.74, 0) * mm, v(2822.75, -50) * mm, v(3321.76, -125) * mm], "startDerivative": vector(1000.33, -87.77) * mm, "endDerivative": vector(995.7, -162.2) * mm});
            skSolve(sketch);
        }
        {
            var Q0;
            Q0=sQuery(id+"F41.wireOp",EDGE,"E100");
            cPlane(context, id + "F59", {"entities" : qUnion([Q0]), "cplaneType" : CPlaneType.LINE_ANGLE, "offset" : 25 * mm, "angle" : 90 * degree, "oppositeDirection" : true, "width" : 150 * mm, "height" : 150 * mm});
        }
        {
            var Q0;
            Q0=qCreatedBy(id+"F59.planeOp",FACE);
            var sketch = newSketch(context, id + "F60", { "sketchPlane" : qUnion([Q0])});
            skFitSpline(sketch, "E130", {"points": [v(1839.3, -18) * mm, v(1039.3, 100) * mm, v(-160.7, -18) * mm], "startDerivative": vector(0, 273.2) * mm, "endDerivative": vector(-3274.07, -98.22) * mm});
            skFitSpline(sketch, "E131", {"points": [v(1839.3, -18) * mm, v(1039.3, -100) * mm, v(-160.7, -18) * mm], "startDerivative": vector(0, -323.44) * mm, "endDerivative": vector(-3271.82, -98.15) * mm});
            skSolve(sketch);
        }
        {
            var Q0;
            Q0=sQuery(id+"F41.wireOp",EDGE,"E112");
            cPlane(context, id + "F61", {"entities" : qUnion([Q0]), "cplaneType" : CPlaneType.LINE_ANGLE, "offset" : 25 * mm, "angle" : 90 * degree, "width" : 150 * mm, "height" : 150 * mm});
        }
        {
            var Q0;
            Q0=qCreatedBy(id+"F61.planeOp",FACE);
            var sketch = newSketch(context, id + "F62", { "sketchPlane" : qUnion([Q0])});
            skFitSpline(sketch, "E132", {"points": [v(-1839.3, -18) * mm, v(-1039.3, 100) * mm, v(160.7, -18) * mm], "startDerivative": vector(0, 273.2) * mm, "endDerivative": vector(3274.07, -98.22) * mm});
            skFitSpline(sketch, "E133", {"points": [v(-1839.3, -18) * mm, v(-1039.3, -100) * mm, v(160.7, -18) * mm], "startDerivative": vector(0, -323.44) * mm, "endDerivative": vector(3271.82, -98.15) * mm});
            skSolve(sketch);
        }
        {
            var Q0;
            Q0 = qSketchRegion(id + "F42", true);
            extrude(context, id + "F63", {"entities" : qUnion([Q0]), "endBound" : BoundingType.SYMMETRIC, "depth" : 2500 * mm, "offsetDistance" : 25 * mm});
        }
        {
            var Q1;
            Q1=makeQuery(id+"F63.opExtrude","CAP_FACE",FACE,{"disambiguationData":[OSD([sQuery(id+"F42.wireOp",EDGE,"E113")])],"isStart":true});
            var Q2;
            {var subQ0=sQuery(id+"F44.wireOp",EDGE,"E114");Q2=makeQuery(id+"F44.imprint","IMPRINT",FACE,{"disambiguationData":[TD([[makeQuery(id+"F44.imprint","IMPRINT",EDGE,{"derivedFrom":subQ0}),-1.0]])]});}
            loft(context, id + "F64", {"operationType" : NewBodyOperationType.ADD, "sheetProfilesArray" : [{ "sheetProfileEntities" : qUnion([Q1]) }, { "sheetProfileEntities" : qUnion([Q2]) }]});
        }
        {
            var Q1;
            Q1=makeQuery(id+"F63.opExtrude","CAP_FACE",FACE,{"disambiguationData":[OSD([sQuery(id+"F42.wireOp",EDGE,"E113")])],"isStart":false});
            var Q2;
            {var subQ0=sQuery(id+"F46.wireOp",EDGE,"E116");Q2=makeQuery(id+"F46.imprint","IMPRINT",FACE,{"disambiguationData":[TD([[makeQuery(id+"F46.imprint","IMPRINT",EDGE,{"derivedFrom":subQ0}),-1.0]])]});}
            loft(context, id + "F65", {"operationType" : NewBodyOperationType.ADD, "sheetProfilesArray" : [{ "sheetProfileEntities" : qUnion([Q1]) }, { "sheetProfileEntities" : qUnion([Q2]) }]});
        }
        {
            var Q1;
            {var subQ0=sQuery(id+"F44.wireOp",EDGE,"E114");Q1=makeQuery(id+"F64.opLoft","CAP_FACE",FACE,{"disambiguationData":[OSD([makeQuery(id+"F44.imprint","IMPRINT",FACE,{"disambiguationData":[TD([[makeQuery(id+"F44.imprint","IMPRINT",EDGE,{"derivedFrom":subQ0}),-1.0]])]})])],"isStart":true});}
            var Q2;
            {var subQ0=sQuery(id+"F48.wireOp",EDGE,"E118");Q2=makeQuery(id+"F48.imprint","IMPRINT",FACE,{"disambiguationData":[TD([[makeQuery(id+"F48.imprint","IMPRINT",EDGE,{"derivedFrom":subQ0}),-1.0]])]});}
            loft(context, id + "F66", {"operationType" : NewBodyOperationType.ADD, "sheetProfilesArray" : [{ "sheetProfileEntities" : qUnion([Q1]) }, { "sheetProfileEntities" : qUnion([Q2]) }]});
        }
        {
            var Q1;
            {var subQ0=sQuery(id+"F46.wireOp",EDGE,"E116");Q1=makeQuery(id+"F65.opLoft","CAP_FACE",FACE,{"disambiguationData":[OSD([makeQuery(id+"F46.imprint","IMPRINT",FACE,{"disambiguationData":[TD([[makeQuery(id+"F46.imprint","IMPRINT",EDGE,{"derivedFrom":subQ0}),-1.0]])]})])],"isStart":true});}
            var Q2;
            {var subQ0=sQuery(id+"F50.wireOp",EDGE,"E120");Q2=makeQuery(id+"F50.imprint","IMPRINT",FACE,{"disambiguationData":[TD([[makeQuery(id+"F50.imprint","IMPRINT",EDGE,{"derivedFrom":subQ0}),-1.0]])]});}
            loft(context, id + "F67", {"operationType" : NewBodyOperationType.ADD, "sheetProfilesArray" : [{ "sheetProfileEntities" : qUnion([Q1]) }, { "sheetProfileEntities" : qUnion([Q2]) }]});
        }
        {
            var Q1;
            {var subQ0=sQuery(id+"F48.wireOp",EDGE,"E118");Q1=makeQuery(id+"F66.opLoft","CAP_FACE",FACE,{"disambiguationData":[OSD([makeQuery(id+"F48.imprint","IMPRINT",FACE,{"disambiguationData":[TD([[makeQuery(id+"F48.imprint","IMPRINT",EDGE,{"derivedFrom":subQ0}),-1.0]])]})])],"isStart":true});}
            var Q2;
            {var subQ0=sQuery(id+"F52.wireOp",EDGE,"E122");Q2=makeQuery(id+"F52.imprint","IMPRINT",FACE,{"disambiguationData":[TD([[makeQuery(id+"F52.imprint","IMPRINT",EDGE,{"derivedFrom":subQ0}),1.0]])]});}
            loft(context, id + "F68", {"operationType" : NewBodyOperationType.ADD, "sheetProfilesArray" : [{ "sheetProfileEntities" : qUnion([Q1]) }, { "sheetProfileEntities" : qUnion([Q2]) }]});
        }
        {
            var Q1;
            {var subQ0=sQuery(id+"F50.wireOp",EDGE,"E120");Q1=makeQuery(id+"F67.opLoft","CAP_FACE",FACE,{"disambiguationData":[OSD([makeQuery(id+"F50.imprint","IMPRINT",FACE,{"disambiguationData":[TD([[makeQuery(id+"F50.imprint","IMPRINT",EDGE,{"derivedFrom":subQ0}),-1.0]])]})])],"isStart":true});}
            var Q2;
            {var subQ0=sQuery(id+"F54.wireOp",EDGE,"E124");Q2=makeQuery(id+"F54.imprint","IMPRINT",FACE,{"disambiguationData":[TD([[makeQuery(id+"F54.imprint","IMPRINT",EDGE,{"derivedFrom":subQ0}),-1.0]])]});}
            loft(context, id + "F69", {"operationType" : NewBodyOperationType.ADD, "sheetProfilesArray" : [{ "sheetProfileEntities" : qUnion([Q1]) }, { "sheetProfileEntities" : qUnion([Q2]) }]});
        }
        {
            var Q1;
            {var subQ0=sQuery(id+"F52.wireOp",EDGE,"E122");Q1=makeQuery(id+"F68.opLoft","CAP_FACE",FACE,{"disambiguationData":[OSD([makeQuery(id+"F52.imprint","IMPRINT",FACE,{"disambiguationData":[TD([[makeQuery(id+"F52.imprint","IMPRINT",EDGE,{"derivedFrom":subQ0}),1.0]])]})])],"isStart":true});}
            var Q2;
            Q2=makeQuery(id+"F56.imprint","IMPRINT",FACE,{"disambiguationData":[TD([[makeQuery(id+"F56.imprint","IMPRINT",EDGE,{"derivedFrom":sQuery(id+"F56.wireOp",EDGE,"E126")}),1.0]])]});
            loft(context, id + "F70", {"operationType" : NewBodyOperationType.ADD, "sheetProfilesArray" : [{ "sheetProfileEntities" : qUnion([Q1]) }, { "sheetProfileEntities" : qUnion([Q2]) }]});
        }
        {
            var Q1;
            {var subQ0=sQuery(id+"F54.wireOp",EDGE,"E124");Q1=makeQuery(id+"F69.opLoft","CAP_FACE",FACE,{"disambiguationData":[OSD([makeQuery(id+"F54.imprint","IMPRINT",FACE,{"disambiguationData":[TD([[makeQuery(id+"F54.imprint","IMPRINT",EDGE,{"derivedFrom":subQ0}),-1.0]])]})])],"isStart":true});}
            var Q2;
            Q2=makeQuery(id+"F58.imprint","IMPRINT",FACE,{"disambiguationData":[TD([[makeQuery(id+"F58.imprint","IMPRINT",EDGE,{"derivedFrom":sQuery(id+"F58.wireOp",EDGE,"E128")}),-1.0]])]});
            loft(context, id + "F71", {"operationType" : NewBodyOperationType.ADD, "sheetProfilesArray" : [{ "sheetProfileEntities" : qUnion([Q1]) }, { "sheetProfileEntities" : qUnion([Q2]) }]});
        }
        {
            var Q1;
            Q1=makeQuery(id+"F70.opLoft","CAP_FACE",FACE,{"disambiguationData":[OSD([makeQuery(id+"F56.imprint","IMPRINT",FACE,{"disambiguationData":[TD([[makeQuery(id+"F56.imprint","IMPRINT",EDGE,{"derivedFrom":sQuery(id+"F56.wireOp",EDGE,"E126")}),1.0]])]})])],"isStart":true});
            var Q2;
            {var subQ0=sQuery(id+"F60.wireOp",EDGE,"E130");Q2=makeQuery(id+"F60.imprint","IMPRINT",FACE,{"disambiguationData":[TD([[makeQuery(id+"F60.imprint","IMPRINT",EDGE,{"derivedFrom":subQ0}),1.0]])]});}
            loft(context, id + "F72", {"operationType" : NewBodyOperationType.ADD, "sheetProfilesArray" : [{ "sheetProfileEntities" : qUnion([Q1]) }, { "sheetProfileEntities" : qUnion([Q2]) }]});
        }
        {
            var Q1;
            Q1=makeQuery(id+"F71.opLoft","CAP_FACE",FACE,{"disambiguationData":[OSD([makeQuery(id+"F58.imprint","IMPRINT",FACE,{"disambiguationData":[TD([[makeQuery(id+"F58.imprint","IMPRINT",EDGE,{"derivedFrom":sQuery(id+"F58.wireOp",EDGE,"E128")}),-1.0]])]})])],"isStart":true});
            var Q2;
            {var subQ0=sQuery(id+"F62.wireOp",EDGE,"E132");Q2=makeQuery(id+"F62.imprint","IMPRINT",FACE,{"disambiguationData":[TD([[makeQuery(id+"F62.imprint","IMPRINT",EDGE,{"derivedFrom":subQ0}),-1.0]])]});}
            loft(context, id + "F73", {"operationType" : NewBodyOperationType.ADD, "sheetProfilesArray" : [{ "sheetProfileEntities" : qUnion([Q1]) }, { "sheetProfileEntities" : qUnion([Q2]) }]});
        }
    });
